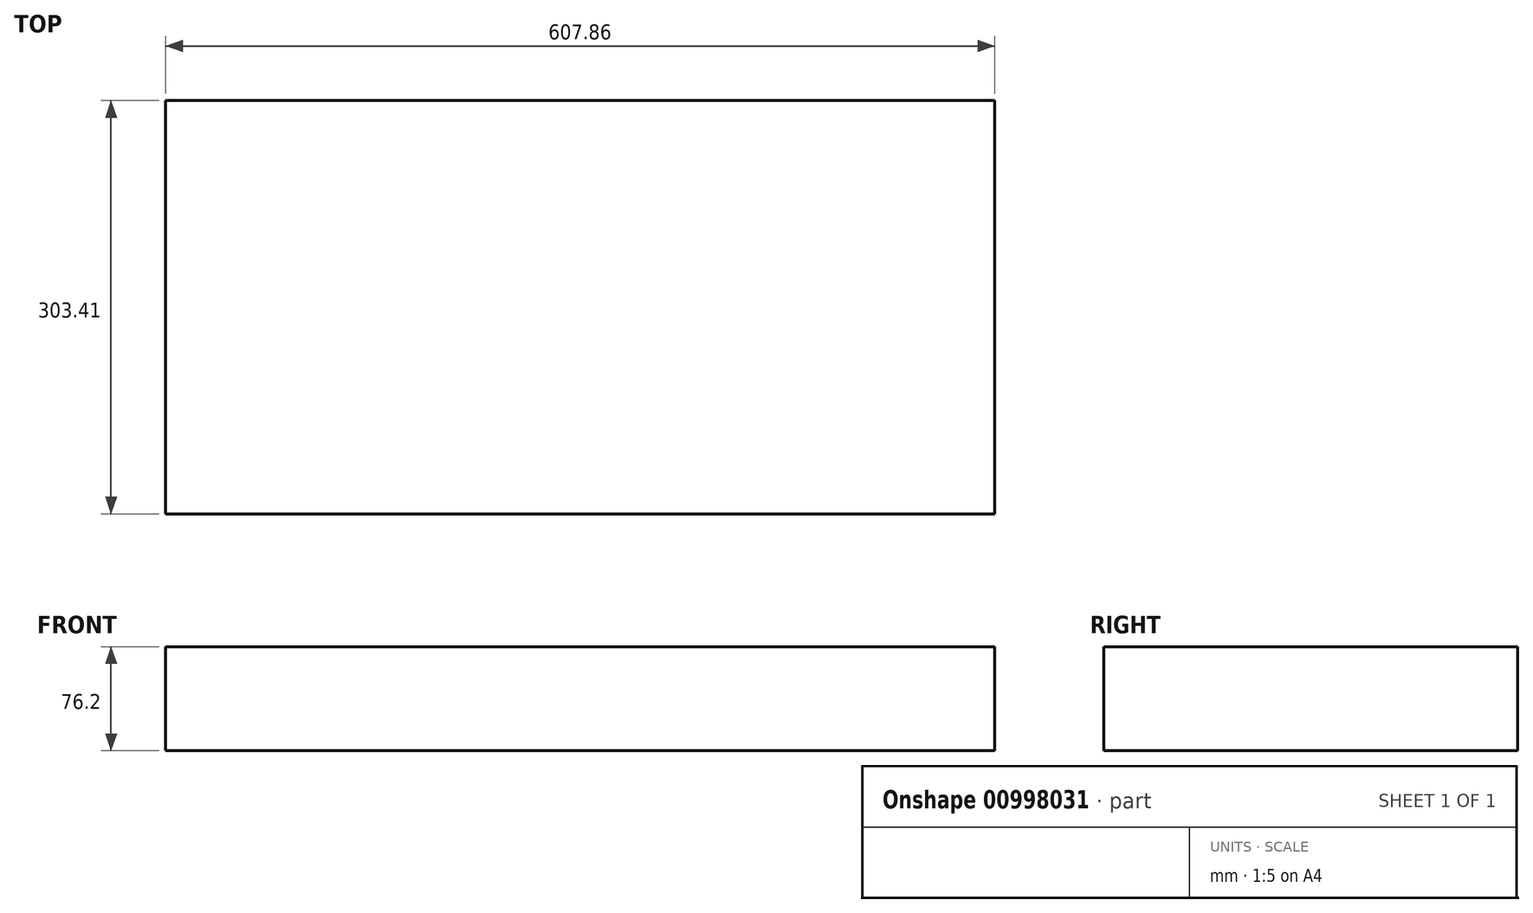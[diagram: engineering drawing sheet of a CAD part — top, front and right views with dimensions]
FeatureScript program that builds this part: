
annotation { "Feature Type Name" : "Feature", "Feature Type Description" : "" }
export const myFeature = defineFeature(function(context is Context, id is Id, definition is map)
    precondition{}
    {
        {
            var Q0;
            Q0=qCreatedBy(makeId("Top.planeOp"),FACE);
            var sketch = newSketch(context, id + "F0", { "sketchPlane" : qUnion([Q0])});
            skLineSegment(sketch, "E0.bottom", {"start": v(-321.1, -134.71) * mm, "end": v(286.76, -134.71) * mm});
            skLineSegment(sketch, "E0.top", {"start": v(-321.1, 168.7) * mm, "end": v(286.76, 168.7) * mm});
            skLineSegment(sketch, "E0.left", {"start": v(-321.1, -134.71) * mm, "end": v(-321.1, 168.7) * mm});
            skLineSegment(sketch, "E0.right", {"start": v(286.76, -134.71) * mm, "end": v(286.76, 168.7) * mm});
            skSolve(sketch);
        }
        {
            var Q0;
            Q0=makeQuery(id+"F0.imprint","IMPRINT",FACE,{"disambiguationData":[TD([[makeQuery(id+"F0.imprint","IMPRINT",EDGE,{"derivedFrom":sQuery(id+"F0.wireOp",EDGE,"E0.bottom")}),1.0]])]});
            extrude(context, id + "F1", {"entities" : qUnion([Q0]), "depth" : 76.2 * mm, "offsetDistance" : 25.4 * mm});
        }
        {
            var Q0;
            Q0=makeQuery(id+"F1.opExtrude","CAP_FACE",FACE,{"disambiguationData":[OSD([sQuery(id+"F0.wireOp",EDGE,"E0.bottom"),sQuery(id+"F0.wireOp",EDGE,"E0.top"),sQuery(id+"F0.wireOp",EDGE,"E0.left"),sQuery(id+"F0.wireOp",EDGE,"E0.right")])],"isStart":false});
            var sketch = newSketch(context, id + "F2", { "sketchPlane" : qUnion([Q0])});
            skLineSegment(sketch, "E1", {"start": v(286.76, -16.34) * mm, "end": v(263.64, -16.34) * mm});
            skLineSegment(sketch, "E2", {"start": v(263.64, -16.34) * mm, "end": v(263.64, -40.07) * mm});
            skLineSegment(sketch, "E3", {"start": v(263.64, -40.07) * mm, "end": v(263.64, -67.2) * mm});
            skLineSegment(sketch, "E4", {"start": v(263.64, -67.2) * mm, "end": v(237.65, -67.2) * mm});
            skLineSegment(sketch, "E5", {"start": v(237.65, -67.2) * mm, "end": v(237.65, 22.08) * mm});
            skLineSegment(sketch, "E6", {"start": v(286.76, 17) * mm, "end": v(260.25, 17) * mm});
            skLineSegment(sketch, "E7", {"start": v(260.25, 17) * mm, "end": v(260.25, 57.1) * mm});
            skLineSegment(sketch, "E8", {"start": v(260.25, 57.1) * mm, "end": v(176.63, 57.1) * mm});
            skLineSegment(sketch, "E9", {"start": v(176.63, 57.1) * mm, "end": v(176.63, -31.03) * mm});
            skLineSegment(sketch, "E10", {"start": v(176.63, -31.03) * mm, "end": v(-321.1, -31.03) * mm});
            skLineSegment(sketch, "E11", {"start": v(237.65, 22.08) * mm, "end": v(203.77, 22.08) * mm});
            skLineSegment(sketch, "E12", {"start": v(203.77, 22.08) * mm, "end": v(203.77, -54.84) * mm});
            skLineSegment(sketch, "E13", {"start": v(203.77, -54.84) * mm, "end": v(-321.1, -54.84) * mm});
            skSolve(sketch);
        }
        {
            var Q0;
            Q0=sQuery(id+"F2.wireOp",EDGE,"E12");
            var Q1;
            Q1=sQuery(id+"F2.wireOp",EDGE,"E6");
            var Q2;
            Q2=sQuery(id+"F2.wireOp",EDGE,"E13");
            var Q3;
            Q3=sQuery(id+"F2.wireOp",EDGE,"E9");
            var Q4;
            Q4=sQuery(id+"F2.wireOp",EDGE,"E2");
            var Q5;
            Q5=sQuery(id+"F2.wireOp",EDGE,"E8");
            var Q6;
            Q6=sQuery(id+"F2.wireOp",EDGE,"E11");
            var Q7;
            Q7=sQuery(id+"F2.wireOp",EDGE,"E5");
            var Q8;
            Q8=sQuery(id+"F2.wireOp",EDGE,"E1");
            var Q9;
            Q9=sQuery(id+"F2.wireOp",EDGE,"E4");
            var Q10;
            Q10=sQuery(id+"F2.wireOp",EDGE,"E3");
            var Q11;
            Q11=sQuery(id+"F2.wireOp",EDGE,"E10");
            var Q12;
            Q12=sQuery(id+"F2.wireOp",EDGE,"E7");
            extrude(context, id + "F3", {"bodyType" : ToolBodyType.SURFACE, "surfaceEntities" : qUnion([Q0, Q1, Q2, Q3, Q4, Q5, Q6, Q7, Q8, Q9, Q10, Q11, Q12]), "depth" : 25.4 * mm, "offsetDistance" : 25.4 * mm});
        }
    });
